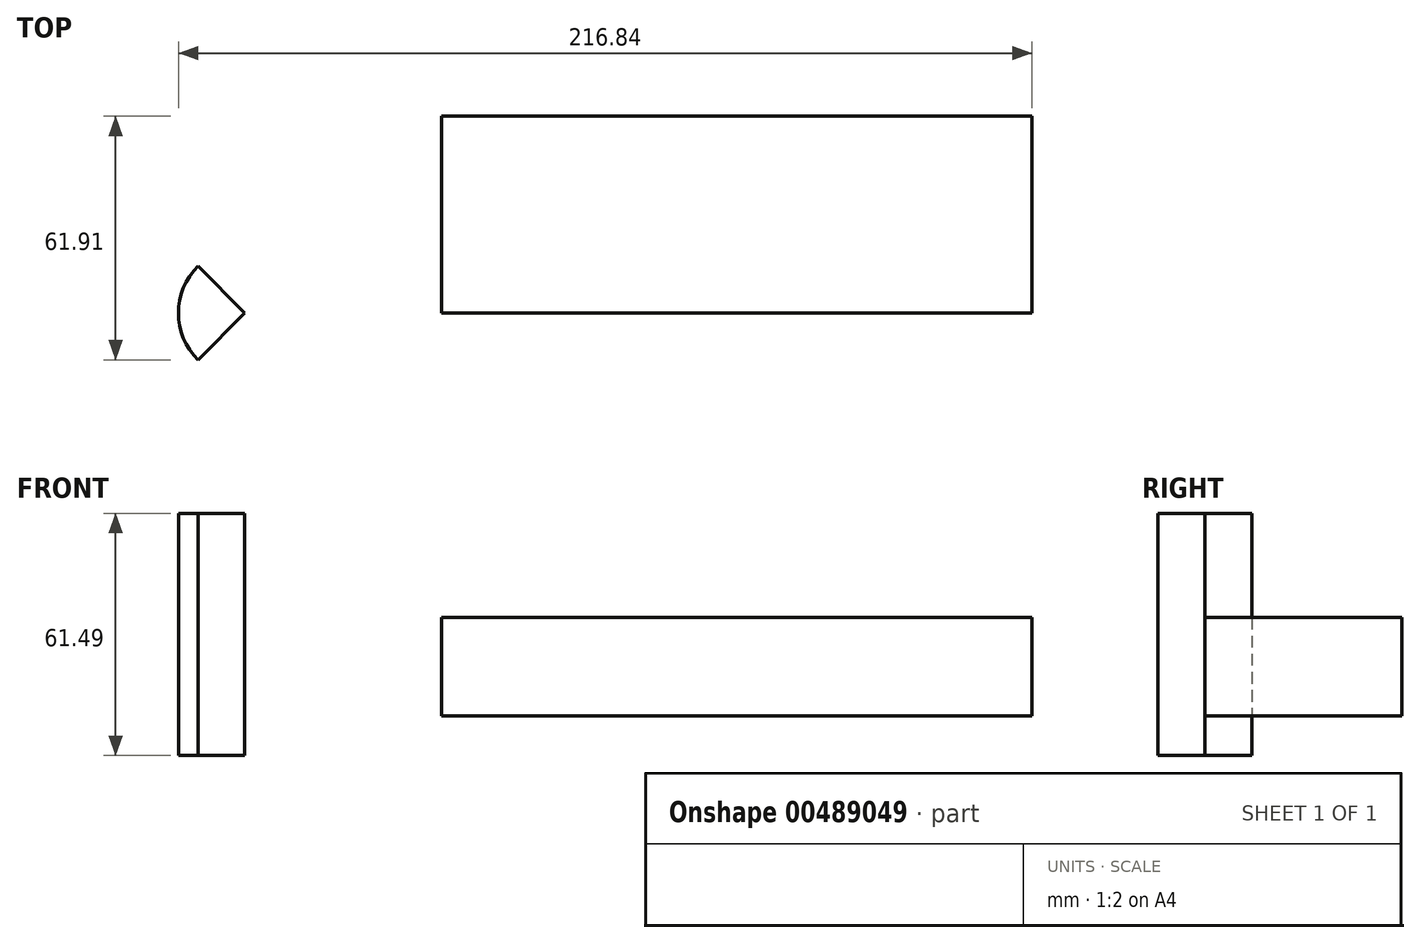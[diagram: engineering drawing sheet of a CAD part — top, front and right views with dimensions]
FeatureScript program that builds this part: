
annotation { "Feature Type Name" : "Feature", "Feature Type Description" : "" }
export const myFeature = defineFeature(function(context is Context, id is Id, definition is map)
    precondition{}
    {
        {
            var Q0;
            Q0=qCreatedBy(makeId("Top.planeOp"),FACE);
            var sketch = newSketch(context, id + "F0", { "sketchPlane" : qUnion([Q0])});
            skLineSegment(sketch, "E0.bottom", {"start": v(0, 0) * mm, "end": v(150, 0) * mm});
            skLineSegment(sketch, "E0.top", {"start": v(0, 50) * mm, "end": v(150, 50) * mm});
            skLineSegment(sketch, "E0.left", {"start": v(0, 0) * mm, "end": v(0, 50) * mm});
            skLineSegment(sketch, "E0.right", {"start": v(150, 0) * mm, "end": v(150, 50) * mm});
            skSolve(sketch);
        }
        {
            var Q0;
            Q0=makeQuery(id+"F0.imprint","IMPRINT",FACE,{"disambiguationData":[TD([[makeQuery(id+"F0.imprint","IMPRINT",EDGE,{"derivedFrom":sQuery(id+"F0.wireOp",EDGE,"E0.bottom")}),1.0]])]});
            extrude(context, id + "F1", {"entities" : qUnion([Q0]), "depth" : 25 * mm});
        }
        {
            var Q0;
            Q0=qCreatedBy(makeId("Front.planeOp"),FACE);
            var sketch = newSketch(context, id + "F2", { "sketchPlane" : qUnion([Q0])});
            skLineSegment(sketch, "E1.bottom", {"start": v(-66.84, 51.5) * mm, "end": v(-50, 51.5) * mm});
            skLineSegment(sketch, "E1.top", {"start": v(-66.84, -10) * mm, "end": v(-50, -10) * mm});
            skLineSegment(sketch, "E1.left", {"start": v(-66.84, 51.5) * mm, "end": v(-66.84, -10) * mm});
            skLineSegment(sketch, "E1.right", {"start": v(-50, 51.5) * mm, "end": v(-50, -10) * mm});
            skSolve(sketch);
        }
        {
            var Q0;
            Q0=makeQuery(id+"F2.imprint","IMPRINT",FACE,{"disambiguationData":[TD([[makeQuery(id+"F2.imprint","IMPRINT",EDGE,{"derivedFrom":sQuery(id+"F2.wireOp",EDGE,"E1.bottom")}),-1.0]])]});
            var Q1;
            Q1=sQuery(id+"F2.wireOp",EDGE,"E1.right");
            revolve(context, id + "F3", {"entities" : qUnion([Q0]), "axis" : qUnion([Q1]), "revolveType" : RevolveType.SYMMETRIC, "angle" : 90 * degree});
        }
    });
